# Revit family: Фильтр-грязевик 2662
name_source: partatom
category: Rohrzubehör
units: mm (PartAtom-declared; Revit-internal decimal feet)

## family parameters
Arbeitsebenenbasiert = Nein
Beim Laden mit Abzugskörper schneiden = Nein
Bemaßung runder Anschluss = Durchmesser verwenden
Gemeinsam genutzt = Nein
Immer vertikal = Ja
OmniClass-Nummer = 23.65.55.14
OmniClass-Titel = Valves for Liquid Services
Teiletyp = Unterbricht

## types (1)
- Фильтр-грязевик 2662
    Hersteller = Herz-Armaturen GmbH
    SCRNCODE = 05;15;02
    SCRNSEQ = AWI;AWI_TYP="1011";2
    SCTWCODE = 04;16;02
    SCTWSEQ = AW;SBT_TYP_AW="112";2
    URL = www.herz-armaturen.ru
    Vorgabe-Ansicht = 0 mm  [stored 0 ft]
    W01 = 45.00°
    Внутренняя резьба = в соответствии с ISO 228-1
    Заглушка = штампованная латунь CW 617N
    Корпус (DN15-DN40) = штампованная латунь CW 617N
    Корпус (DN50) = литая латунь в соотв. с EN 1982; CC770S
    Макс. рабочая температура = 130 °C
    Макс. рабочая температура (вода) = 95 °C
    Макс. рабочее давление = 2500000.0 Pa
    Мин. рабочая температура = -30 °C
    Мин. рабочая температура (вода) = 1 °C
    Область применения = Фильтры устанавливаются с целью защиты клапанов от мелких частиц грязи в системах отопления и 
холодоснабжения. Ароматические хлорированные углеводороды, такие как природный газ или продукты нефтепереработки, разрушают уплотнения из EPDM.
    Среда = Качество теплоносителя в соответствии с ÖNORM H5195 и/или предписаниями VDI-Standard 2035. 
Разрешается использование смеси этилен или пропиленгликоля в соотношении 25-50% с водой. Пожалуйста, обратитесь к документации производителя, при использовании этиленгликоля и пропиленгликоля в целях защиты от замерзания. Прокладки EPDM могут быть подвержены воздействию минеральных смазочных масел, что может служить причиной выхода из строя данных уплотнений.
    Уплотнения = EPDM
    Фильтрующий элемент = нержавеющая сталь, размер ячейки 0,5 мм

note: [stored X ft] marks values corroborated as IEEE doubles in the binary element streams (Revit-internal decimal feet)
